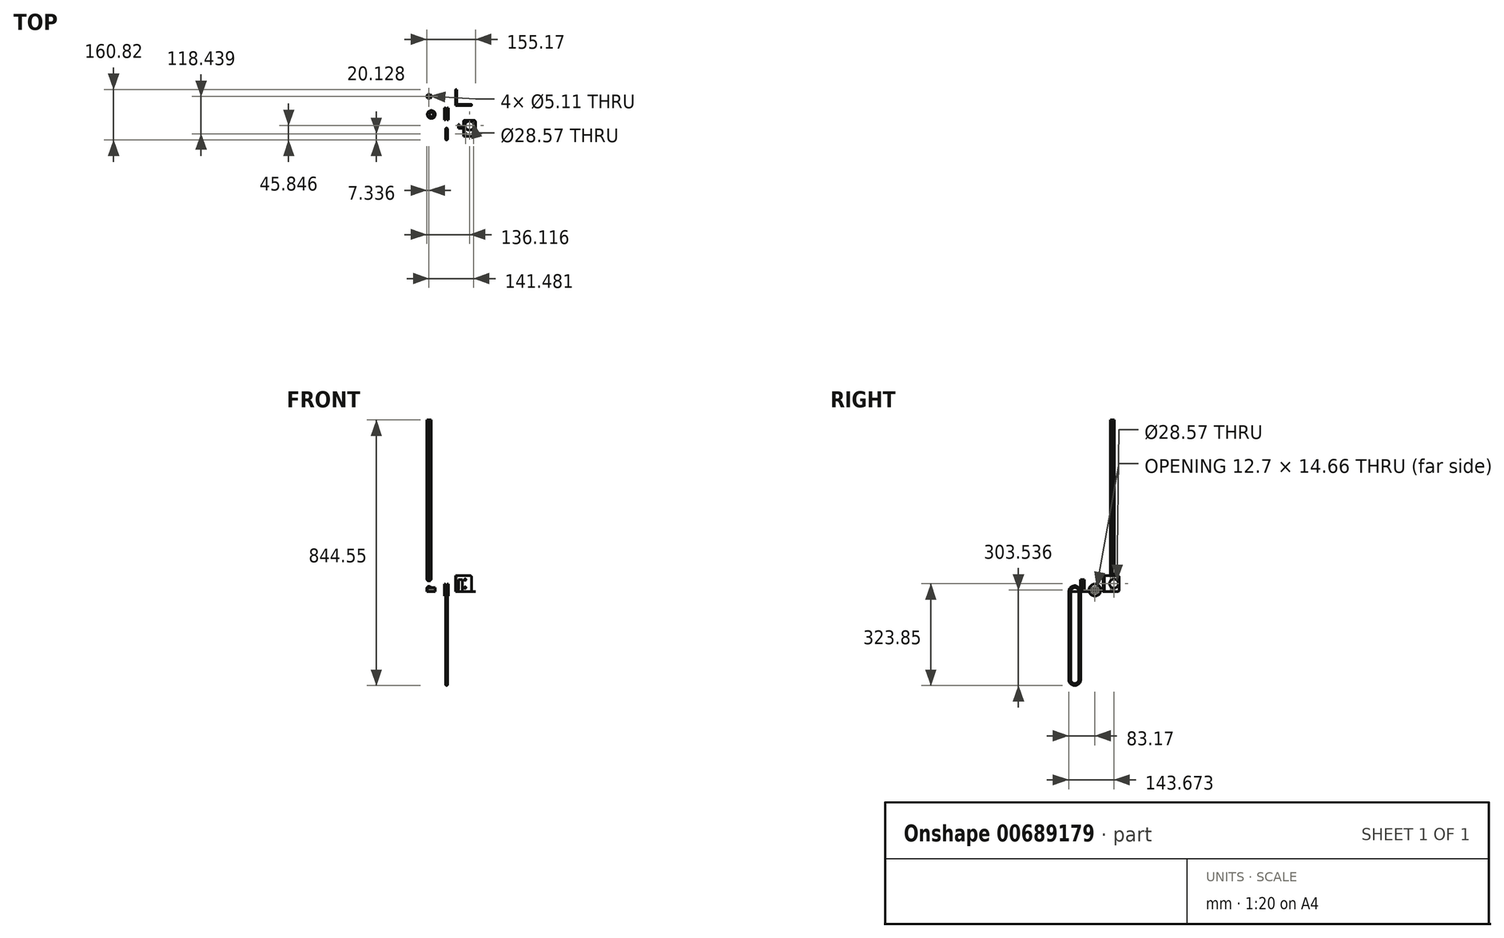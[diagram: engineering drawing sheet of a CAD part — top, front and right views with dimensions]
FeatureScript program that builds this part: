
annotation { "Feature Type Name" : "Feature", "Feature Type Description" : "" }
export const myFeature = defineFeature(function(context is Context, id is Id, definition is map)
    precondition{}
    {
        {
            var Q0;
            Q0=qCreatedBy(makeId("Top.planeOp"),FACE);
            var sketch = newSketch(context, id + "F0", { "sketchPlane" : qUnion([Q0])});
            skCircle(sketch, "E0", {"center": v(-55.88, 55.4) * mm, "radius": 2.55 * mm});
            skCircle(sketch, "E1.cCircle", {"center": v(-55.88, 55.4) * mm, "radius": 6.35 * mm, "construction": true});
            skLineSegment(sketch, "E1.0", {"start": v(-52.25, 49.03) * mm, "end": v(-59.58, 49.06) * mm});
            skLineSegment(sketch, "E1.1", {"start": v(-59.58, 49.06) * mm, "end": v(-63.22, 55.43) * mm});
            skLineSegment(sketch, "E1.2", {"start": v(-63.22, 55.43) * mm, "end": v(-59.52, 61.76) * mm});
            skLineSegment(sketch, "E1.3", {"start": v(-59.52, 61.76) * mm, "end": v(-52.19, 61.73) * mm});
            skLineSegment(sketch, "E1.4", {"start": v(-52.19, 61.73) * mm, "end": v(-48.55, 55.36) * mm});
            skLineSegment(sketch, "E1.5", {"start": v(-48.55, 55.36) * mm, "end": v(-52.25, 49.03) * mm});
            skPoint(sketch, "E1.0.midPoint", {"position": v(-55.91, 49.05) * mm});
            skSolve(sketch);
        }
        {
            var Q0;
            Q0=makeQuery(id+"F0.imprint","IMPRINT",FACE,{"disambiguationData":[TD([[makeQuery(id+"F0.imprint","IMPRINT",EDGE,{"derivedFrom":sQuery(id+"F0.wireOp",EDGE,"E0")}),-1.0]])]});
            extrude(context, id + "F1", {"entities" : qUnion([Q0]), "depth" : 546.1 * mm, "offsetDistance" : 25.4 * mm});
        }
        {
            var Q0;
            Q0=qCreatedBy(makeId("Front.planeOp"),FACE);
            var sketch = newSketch(context, id + "F2", { "sketchPlane" : qUnion([Q0])});
            skLineSegment(sketch, "E2", {"start": v(-6.83, 5.09) * mm, "end": v(-6.83, 24.14) * mm});
            skLineSegment(sketch, "E3", {"start": v(-6.83, 24.14) * mm, "end": v(-3.66, 24.14) * mm});
            skArc(sketch, "E4", {"start": v(-3.66, 20.96) * mm, "mid": v(-0.48, 17.79) * mm, "end": v(2.7, 20.96) * mm});
            skLineSegment(sketch, "E5", {"start": v(-3.66, 24.14) * mm, "end": v(-3.66, 20.96) * mm});
            skLineSegment(sketch, "E6", {"start": v(2.7, 20.96) * mm, "end": v(2.7, 24.14) * mm});
            skLineSegment(sketch, "E7", {"start": v(2.7, 24.14) * mm, "end": v(5.87, 24.14) * mm});
            skLineSegment(sketch, "E8", {"start": v(5.87, 24.14) * mm, "end": v(5.87, 5.09) * mm});
            skLineSegment(sketch, "E9", {"start": v(5.87, 5.09) * mm, "end": v(-6.83, 5.09) * mm});
            skCircle(sketch, "E10", {"center": v(-0.48, 20.96) * mm, "radius": 3.18 * mm, "construction": true});
            skLineSegment(sketch, "E11", {"start": v(-3.66, 24.14) * mm, "end": v(2.7, 24.14) * mm, "construction": true});
            skLineSegment(sketch, "E12", {"start": v(-0.48, 20.96) * mm, "end": v(-0.48, -6.23) * mm, "construction": true});
            skSolve(sketch);
        }
        {
            var Q0;
            Q0=makeQuery(id+"F2.imprint","IMPRINT",FACE,{"disambiguationData":[TD([[makeQuery(id+"F2.imprint","IMPRINT",EDGE,{"derivedFrom":sQuery(id+"F2.wireOp",EDGE,"E2")}),-1.0]])]});
            var Q1;
            Q1=sQuery(id+"F2.wireOp",EDGE,"E9");
            revolve(context, id + "F3", {"surfaceOperationType" : NewSurfaceOperationType.NEW, "entities" : qUnion([Q0]), "axis" : qUnion([Q1]), "revolveType" : RevolveType.FULL});
        }
        {
            var Q0;
            Q0=makeQuery(id+"F3.opRevolve","SWEPT_FACE",FACE,{"disambiguationData":[OSD([sQuery(id+"F2.wireOp",EDGE,"E8")])]});
            var sketch = newSketch(context, id + "F4", { "sketchPlane" : qUnion([Q0])});
            skCircle(sketch, "E13.0.0", {"center": v(0, 5.09) * mm, "radius": 19.05 * mm, "construction": true});
            skCircle(sketch, "E14.cCircle", {"center": v(0, 5.09) * mm, "radius": 6.35 * mm, "construction": true});
            skLineSegment(sketch, "E14.0", {"start": v(-6.35, 8.75) * mm, "end": v(0, 12.42) * mm});
            skLineSegment(sketch, "E14.1", {"start": v(0, 12.42) * mm, "end": v(6.35, 8.75) * mm});
            skLineSegment(sketch, "E14.2", {"start": v(6.35, 8.75) * mm, "end": v(6.35, 1.42) * mm});
            skLineSegment(sketch, "E14.3", {"start": v(6.35, 1.42) * mm, "end": v(0, -2.25) * mm});
            skLineSegment(sketch, "E14.4", {"start": v(0, -2.25) * mm, "end": v(-6.35, 1.42) * mm});
            skLineSegment(sketch, "E14.5", {"start": v(-6.35, 1.42) * mm, "end": v(-6.35, 8.75) * mm});
            skPoint(sketch, "E14.0.midPoint", {"position": v(-3.18, 10.59) * mm});
            skSolve(sketch);
        }
        {
            var Q0;
            Q0=makeQuery(id+"F4.imprint","IMPRINT",FACE,{"disambiguationData":[TD([[makeQuery(id+"F4.imprint","IMPRINT",EDGE,{"derivedFrom":sQuery(id+"F4.wireOp",EDGE,"E14.0")}),-1.0]])]});
            extrude(context, id + "F5", {"entities" : qUnion([Q0]), "operationType" : NewBodyOperationType.REMOVE, "endBound" : BoundingType.THROUGH_ALL, "oppositeDirection" : true, "depth" : 25.4 * mm, "offsetDistance" : 25.4 * mm});
        }
        {
            var Q0;
            Q0=makeQuery(id+"F3.opRevolve","SWEPT_EDGE",EDGE,{"disambiguationData":[OSD([sQuery(id+"F2.wireOp",EDGE,"E3"),sQuery(id+"F2.wireOp",EDGE,"E5")])]});
            var Q1;
            Q1=makeQuery(id+"F3.opRevolve","SWEPT_EDGE",EDGE,{"disambiguationData":[OSD([sQuery(id+"F2.wireOp",EDGE,"E6"),sQuery(id+"F2.wireOp",EDGE,"E7")])]});
            fillet(context, id + "F6", {"entities" : qUnion([Q0, Q1]), "radius" : 0.64 * mm, "tangentPropagation" : true, "allowEdgeOverflow" : false});
        }
        {
            var Q0;
            Q0=qCreatedBy(makeId("Top.planeOp"),FACE);
            var sketch = newSketch(context, id + "F7", { "sketchPlane" : qUnion([Q0])});
            skCircle(sketch, "E15", {"center": v(-48.4, -1.9) * mm, "radius": 12.7 * mm});
            skCircle(sketch, "E16.cCircle", {"center": v(-48.4, -1.9) * mm, "radius": 6.35 * mm, "construction": true});
            skLineSegment(sketch, "E16.0", {"start": v(-51.08, -8.73) * mm, "end": v(-55.65, -3) * mm});
            skLineSegment(sketch, "E16.1", {"start": v(-55.65, -3) * mm, "end": v(-52.97, 3.83) * mm});
            skLineSegment(sketch, "E16.2", {"start": v(-52.97, 3.83) * mm, "end": v(-45.71, 4.92) * mm});
            skLineSegment(sketch, "E16.3", {"start": v(-45.71, 4.92) * mm, "end": v(-41.15, -0.82) * mm});
            skLineSegment(sketch, "E16.4", {"start": v(-41.15, -0.82) * mm, "end": v(-43.83, -7.64) * mm});
            skLineSegment(sketch, "E16.5", {"start": v(-43.83, -7.64) * mm, "end": v(-51.08, -8.73) * mm});
            skPoint(sketch, "E16.0.midPoint", {"position": v(-53.36, -5.86) * mm});
            skSolve(sketch);
        }
        {
            var Q0;
            Q0=makeQuery(id+"F7.imprint","IMPRINT",FACE,{"disambiguationData":[TD([[makeQuery(id+"F7.imprint","IMPRINT",EDGE,{"derivedFrom":sQuery(id+"F7.wireOp",EDGE,"E15")}),1.0]])]});
            extrude(context, id + "F8", {"entities" : qUnion([Q0]), "depth" : 12.7 * mm, "offsetDistance" : 25.4 * mm});
        }
        {
            var Q0;
            Q0=qCreatedBy(makeId("Right.planeOp"),FACE);
            var sketch = newSketch(context, id + "F9", { "sketchPlane" : qUnion([Q0])});
            skLineSegment(sketch, "E17", {"start": v(-64.12, 0) * mm, "end": v(-64.12, -279.4) * mm, "construction": true});
            skArc(sketch, "E18.0.startCap", {"start": v(-80, 0) * mm, "mid": v(-64.12, 15.87) * mm, "end": v(-48.25, 0) * mm});
            skArc(sketch, "E18.0.endCap", {"start": v(-48.25, -279.4) * mm, "mid": v(-64.12, -295.28) * mm, "end": v(-80, -279.4) * mm});
            skLineSegment(sketch, "E18.0.left", {"start": v(-48.25, 0) * mm, "end": v(-48.25, -279.4) * mm});
            skLineSegment(sketch, "E18.0.right", {"start": v(-80, 0) * mm, "end": v(-80, -279.4) * mm});
            skSolve(sketch);
        }
        {
            var Q0;
            Q0=qCreatedBy(makeId("Top.planeOp"),FACE);
            var sketch = newSketch(context, id + "F10", { "sketchPlane" : qUnion([Q0])});
            skPoint(sketch, "E19.0", {"position": v(0, -80) * mm});
            skCircle(sketch, "E20", {"center": v(0, -80) * mm, "radius": 3.18 * mm});
            skSolve(sketch);
        }
        {
            var Q0;
            Q0=makeQuery(id+"F10.imprint","IMPRINT",FACE,{"disambiguationData":[TD([[makeQuery(id+"F10.imprint","IMPRINT",EDGE,{"derivedFrom":sQuery(id+"F10.wireOp",EDGE,"E20")}),1.0]])]});
            var Q1;
            Q1=sQuery(id+"F9.wireOp",EDGE,"E18.0.startCap");
            var Q2;
            Q2=sQuery(id+"F9.wireOp",EDGE,"E18.0.left");
            var Q3;
            Q3=sQuery(id+"F9.wireOp",EDGE,"E18.0.endCap");
            var Q4;
            Q4=sQuery(id+"F9.wireOp",EDGE,"E18.0.right");
            sweep(context, id + "F11", {"profiles" : qUnion([Q0]), "path" : qUnion([Q1, Q2, Q3, Q4])});
        }
        {
            var Q0;
            Q0=qCreatedBy(makeId("Top.planeOp"),FACE);
            var sketch = newSketch(context, id + "F12", { "sketchPlane" : qUnion([Q0])});
            skLineSegment(sketch, "E21", {"start": v(29.14, 77.65) * mm, "end": v(29.14, 26.85) * mm});
            skLineSegment(sketch, "E22", {"start": v(29.14, 26.85) * mm, "end": v(79.94, 26.85) * mm});
            skLineSegment(sketch, "E23", {"start": v(79.94, 26.85) * mm, "end": v(79.94, 30.02) * mm});
            skLineSegment(sketch, "E24", {"start": v(79.94, 30.02) * mm, "end": v(38.67, 30.02) * mm});
            skLineSegment(sketch, "E25", {"start": v(32.32, 36.37) * mm, "end": v(32.32, 77.65) * mm});
            skLineSegment(sketch, "E26", {"start": v(32.32, 77.65) * mm, "end": v(29.14, 77.65) * mm});
            skPoint(sketch, "E27.visualSharp", {"position": v(32.32, 30.02) * mm});
            skArc(sketch, "E27.filletArc", {"start": v(32.32, 36.37) * mm, "mid": v(34.18, 31.88) * mm, "end": v(38.67, 30.02) * mm});
            skSolve(sketch);
        }
        {
            var Q0;
            Q0=makeQuery(id+"F12.imprint","IMPRINT",FACE,{"disambiguationData":[TD([[makeQuery(id+"F12.imprint","IMPRINT",EDGE,{"derivedFrom":sQuery(id+"F12.wireOp",EDGE,"E21")}),1.0]])]});
            extrude(context, id + "F13", {"entities" : qUnion([Q0]), "depth" : 50.8 * mm, "offsetDistance" : 25.4 * mm});
        }
        {
            var Q0;
            Q0=makeQuery(id+"F13.opExtrude","SWEPT_FACE",FACE,{"disambiguationData":[OSD([sQuery(id+"F12.wireOp",EDGE,"E25")])]});
            var sketch = newSketch(context, id + "F14", { "sketchPlane" : qUnion([Q0])});
            skCircle(sketch, "E28", {"center": v(60.5, 25.4) * mm, "radius": 14.29 * mm});
            skLineSegment(sketch, "E29.0", {"start": v(77.65, 50.8) * mm, "end": v(77.65, 0) * mm});
            skPoint(sketch, "E30.0", {"position": v(77.65, 25.4) * mm});
            skSolve(sketch);
        }
        {
            var Q0;
            Q0=makeQuery(id+"F13.opExtrude","SWEPT_FACE",FACE,{"disambiguationData":[OSD([sQuery(id+"F12.wireOp",EDGE,"E24")])]});
            var sketch = newSketch(context, id + "F15", { "sketchPlane" : qUnion([Q0])});
            skCircle(sketch, "E31", {"center": v(-59.3, 38.1) * mm, "radius": 2.55 * mm});
            skPoint(sketch, "E31.centerSnap0", {"position": v(-59.3, 50.8) * mm});
            skCircle(sketch, "E32", {"center": v(-59.3, 12.7) * mm, "radius": 2.55 * mm});
            skLineSegment(sketch, "E33", {"start": v(-59.3, 12.7) * mm, "end": v(-59.3, 0) * mm, "construction": true});
            skLineSegment(sketch, "E34", {"start": v(-59.3, 38.1) * mm, "end": v(-59.3, 50.8) * mm, "construction": true});
            skSolve(sketch);
        }
        {
            var Q0;
            Q0 = qSketchRegion(id + "F15", true);
            extrude(context, id + "F16", {"entities" : qUnion([Q0]), "operationType" : NewBodyOperationType.REMOVE, "endBound" : BoundingType.THROUGH_ALL, "oppositeDirection" : true, "depth" : 25.4 * mm, "offsetDistance" : 25.4 * mm});
        }
        {
            var Q0;
            Q0 = qSketchRegion(id + "F14", true);
            extrude(context, id + "F17", {"entities" : qUnion([Q0]), "operationType" : NewBodyOperationType.REMOVE, "endBound" : BoundingType.THROUGH_ALL, "oppositeDirection" : true, "depth" : 25.4 * mm, "offsetDistance" : 25.4 * mm});
        }
        {
            var Q0;
            Q0=makeQuery(id+"F13.opExtrude","CAP_EDGE",EDGE,{"disambiguationData":[OSD([sQuery(id+"F12.wireOp",EDGE,"E26")])],"isStart":false});
            var Q1;
            Q1=makeQuery(id+"F13.opExtrude","CAP_EDGE",EDGE,{"disambiguationData":[OSD([sQuery(id+"F12.wireOp",EDGE,"E26")])],"isStart":true});
            var Q2;
            Q2=makeQuery(id+"F13.opExtrude","CAP_EDGE",EDGE,{"disambiguationData":[OSD([sQuery(id+"F12.wireOp",EDGE,"E23")])],"isStart":false});
            var Q3;
            Q3=makeQuery(id+"F13.opExtrude","CAP_EDGE",EDGE,{"disambiguationData":[OSD([sQuery(id+"F12.wireOp",EDGE,"E23")])],"isStart":true});
            fillet(context, id + "F18", {"entities" : qUnion([Q0, Q1, Q2, Q3]), "radius" : 5.08 * mm, "tangentPropagation" : true, "allowEdgeOverflow" : false});
        }
        {
            var Q0;
            Q0=qCreatedBy(makeId("Top.planeOp"),FACE);
            var sketch = newSketch(context, id + "F19", { "sketchPlane" : qUnion([Q0])});
            skLineSegment(sketch, "E35", {"start": v(37.6, -33.23) * mm, "end": v(37.6, -45.93) * mm});
            skLineSegment(sketch, "E36", {"start": v(37.6, -45.93) * mm, "end": v(50.3, -45.93) * mm});
            skLineSegment(sketch, "E37", {"start": v(50.3, -45.93) * mm, "end": v(50.3, -42.76) * mm});
            skLineSegment(sketch, "E38", {"start": v(50.3, -42.76) * mm, "end": v(40.77, -42.76) * mm});
            skLineSegment(sketch, "E39", {"start": v(40.77, -42.76) * mm, "end": v(40.77, -33.23) * mm});
            skLineSegment(sketch, "E40", {"start": v(40.77, -33.23) * mm, "end": v(37.6, -33.23) * mm});
            skSolve(sketch);
        }
        {
            var Q0;
            Q0=makeQuery(id+"F19.imprint","IMPRINT",FACE,{"disambiguationData":[TD([[makeQuery(id+"F19.imprint","IMPRINT",EDGE,{"derivedFrom":sQuery(id+"F19.wireOp",EDGE,"E35")}),1.0]])]});
            extrude(context, id + "F20", {"entities" : qUnion([Q0]), "depth" : 38.1 * mm, "offsetDistance" : 25.4 * mm});
        }
        {
            var Q0;
            Q0=makeQuery(id+"F20.opExtrude","SWEPT_FACE",FACE,{"disambiguationData":[OSD([sQuery(id+"F19.wireOp",EDGE,"E39")])]});
            var sketch = newSketch(context, id + "F21", { "sketchPlane" : qUnion([Q0])});
            skLineSegment(sketch, "E41.0.0", {"start": v(-42.76, 0) * mm, "end": v(-33.23, 0) * mm, "construction": true});
            skLineSegment(sketch, "E41.0.1", {"start": v(-33.23, 0) * mm, "end": v(-33.23, 38.1) * mm, "construction": true});
            skLineSegment(sketch, "E41.0.2", {"start": v(-33.23, 38.1) * mm, "end": v(-42.76, 38.1) * mm, "construction": true});
            skLineSegment(sketch, "E41.0.3", {"start": v(-42.76, 38.1) * mm, "end": v(-42.76, 0) * mm, "construction": true});
            skCircle(sketch, "E42", {"center": v(-38, 31.75) * mm, "radius": 2.55 * mm});
            skPoint(sketch, "E42.centerSnap0", {"position": v(-38, 38.1) * mm});
            skCircle(sketch, "E43", {"center": v(-38, 6.35) * mm, "radius": 2.55 * mm});
            skLineSegment(sketch, "E44", {"start": v(-38, 31.75) * mm, "end": v(-38, 6.35) * mm, "construction": true});
            skPoint(sketch, "E45", {"position": v(-38, 19.05) * mm});
            skPoint(sketch, "E46", {"position": v(-33.23, 19.05) * mm});
            skSolve(sketch);
        }
        {
            var Q0;
            Q0 = qSketchRegion(id + "F21", true);
            extrude(context, id + "F22", {"entities" : qUnion([Q0]), "operationType" : NewBodyOperationType.REMOVE, "endBound" : BoundingType.THROUGH_ALL, "oppositeDirection" : true, "depth" : 25.4 * mm, "offsetDistance" : 25.4 * mm});
        }
        {
            var Q0;
            Q0=qCreatedBy(makeId("Top.planeOp"),FACE);
            var sketch = newSketch(context, id + "F23", { "sketchPlane" : qUnion([Q0])});
            skLineSegment(sketch, "E47.bottom", {"start": v(53.85, -20.18) * mm, "end": v(91.95, -20.18) * mm});
            skLineSegment(sketch, "E47.top", {"start": v(53.85, -70.98) * mm, "end": v(91.95, -70.98) * mm});
            skLineSegment(sketch, "E47.left", {"start": v(53.85, -20.18) * mm, "end": v(53.85, -70.98) * mm});
            skLineSegment(sketch, "E47.right", {"start": v(91.95, -20.18) * mm, "end": v(91.95, -70.98) * mm});
            skPoint(sketch, "E47.middle", {"position": v(72.9, -45.58) * mm});
            skCircle(sketch, "E48", {"center": v(72.9, -37.32) * mm, "radius": 14.29 * mm});
            skLineSegment(sketch, "E49", {"start": v(60.2, -63.04) * mm, "end": v(85.6, -63.04) * mm, "construction": true});
            skCircle(sketch, "E50", {"center": v(85.6, -63.04) * mm, "radius": 2.55 * mm});
            skCircle(sketch, "E51", {"center": v(60.2, -63.04) * mm, "radius": 2.55 * mm});
            skPoint(sketch, "E52", {"position": v(72.9, -63.04) * mm});
            skPoint(sketch, "E53", {"position": v(72.9, -70.98) * mm});
            skSolve(sketch);
        }
        {
            var Q0;
            Q0=makeQuery(id+"F23.imprint","IMPRINT",FACE,{"disambiguationData":[TD([[makeQuery(id+"F23.imprint","IMPRINT",EDGE,{"derivedFrom":sQuery(id+"F23.wireOp",EDGE,"E47.bottom")}),-1.0]])]});
            extrude(context, id + "F24", {"entities" : qUnion([Q0]), "depth" : 3 / 203.2 * mm, "offsetDistance" : 25.4 * mm});
        }
        {
            var Q0;
            Q0=makeQuery(id+"F24.opExtrude","SWEPT_EDGE",EDGE,{"disambiguationData":[OSD([sQuery(id+"F23.wireOp",EDGE,"E47.bottom"),sQuery(id+"F23.wireOp",EDGE,"E47.left")])]});
            var Q1;
            Q1=makeQuery(id+"F24.opExtrude","SWEPT_EDGE",EDGE,{"disambiguationData":[OSD([sQuery(id+"F23.wireOp",EDGE,"E47.bottom"),sQuery(id+"F23.wireOp",EDGE,"E47.right")])]});
            fillet(context, id + "F25", {"entities" : qUnion([Q0, Q1]), "radius" : 5.08 * mm, "tangentPropagation" : true, "allowEdgeOverflow" : false});
        }
    });
